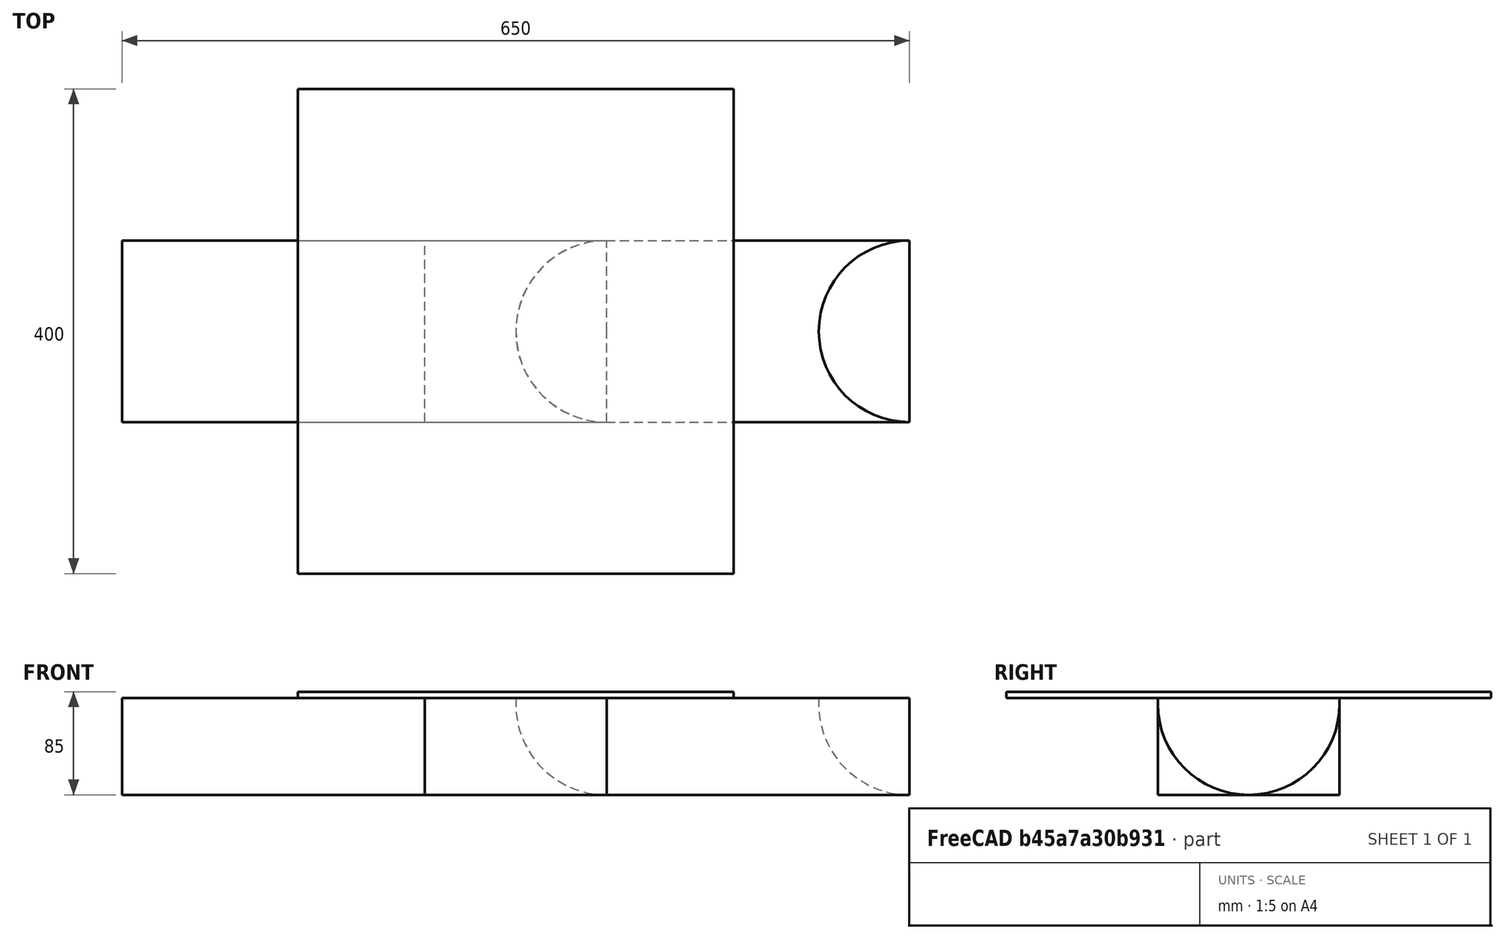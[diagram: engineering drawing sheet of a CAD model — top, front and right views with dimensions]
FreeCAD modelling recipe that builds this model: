
FCSTD DOCUMENT  (FreeCAD 0.19R)
Label: fishing_drone_hull
License: All rights reserved
LicenseURL: http://en.wikipedia.org/wiki/All_rights_reserved
objects: Part::Box×3, Part::Sphere×2, Part::MultiFuse×2
note: 7 computed .brp shape members not serialized (recipe doc carries the construction recipe); baked Part::Feature solids carry a one-line shape summary decoded from their .brp

FEATURE [Part::Box] Pontoon_Left
  AttacherType = Attacher::AttachEngine3D
  Height = 80
  Length = 400
  Placement = pos=(-325,-75,0) rot=(0,0,1;0rad)
  Width = 150
FEATURE [Part::Sphere] Nose_Left
  Angle1 = -90
  Angle2 = 90
  Angle3 = 360
  AttacherType = Attacher::AttachEngine3D
  Placement = pos=(75,0,75) rot=(0,0,1;0rad)
  Radius = 75
FEATURE [Part::MultiFuse] PontoonFused_Left
  Shapes = -> [Pontoon_Left,Nose_Left]
FEATURE [Part::Box] Pontoon_Right
  AttacherType = Attacher::AttachEngine3D
  Height = 80
  Length = 400
  Placement = pos=(-75,-75,0) rot=(0,0,1;0rad)
  Width = 150
FEATURE [Part::Sphere] Nose_Right
  Angle1 = -90
  Angle2 = 90
  Angle3 = 360
  AttacherType = Attacher::AttachEngine3D
  Placement = pos=(325,0,75) rot=(0,0,1;0rad)
  Radius = 75
FEATURE [Part::MultiFuse] PontoonFused_Right
  Shapes = -> [Pontoon_Right,Nose_Right]
FEATURE [Part::Box] Deck
  AttacherType = Attacher::AttachEngine3D
  Height = 5
  Length = 360
  Placement = pos=(-180,-200,80) rot=(0,0,1;0rad)
  Width = 400
